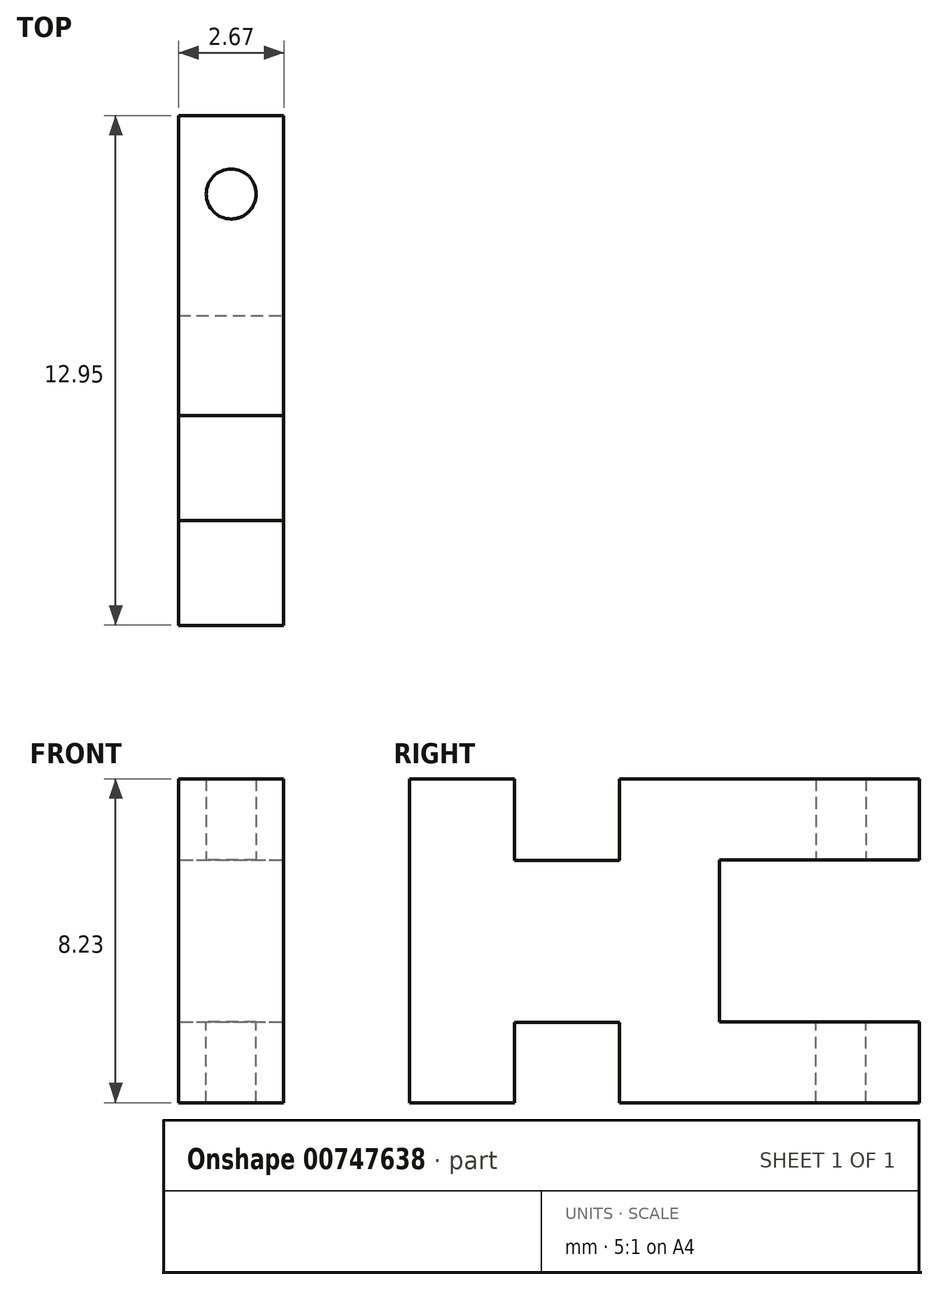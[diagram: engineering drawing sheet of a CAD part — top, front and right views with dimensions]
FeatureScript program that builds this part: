
annotation { "Feature Type Name" : "Feature", "Feature Type Description" : "" }
export const myFeature = defineFeature(function(context is Context, id is Id, definition is map)
    precondition{}
    {
        {
            var Q0;
            Q0=qCreatedBy(makeId("Right.planeOp"),FACE);
            var sketch = newSketch(context, id + "F0", { "sketchPlane" : qUnion([Q0])});
            skLineSegment(sketch, "E0.bottom", {"start": v(-1.33, 2.06) * mm, "end": v(1.33, 2.06) * mm});
            skLineSegment(sketch, "E0.top", {"start": v(-1.33, -2.06) * mm, "end": v(1.33, -2.06) * mm});
            skPoint(sketch, "E0.middle", {"position": v(0, 0) * mm});
            skLineSegment(sketch, "E1.bottom", {"start": v(-1.33, 4.13) * mm, "end": v(-4, 4.13) * mm});
            skLineSegment(sketch, "E1.top", {"start": v(-1.33, -4.1) * mm, "end": v(-4, -4.1) * mm});
            skLineSegment(sketch, "E1.left", {"start": v(-1.33, 4.13) * mm, "end": v(-1.33, 2.06) * mm});
            skLineSegment(sketch, "E1.right", {"start": v(-4, 4.13) * mm, "end": v(-4, -4.1) * mm});
            skPoint(sketch, "E2.firstSnap0", {"position": v(1.33, 0) * mm});
            skLineSegment(sketch, "E2.bottom", {"start": v(1.33, 4.13) * mm, "end": v(8.95, 4.13) * mm});
            skLineSegment(sketch, "E2.top", {"start": v(1.33, -4.1) * mm, "end": v(8.95, -4.1) * mm});
            skLineSegment(sketch, "E2.left", {"start": v(1.33, 4.13) * mm, "end": v(1.33, 2.06) * mm});
            skLineSegment(sketch, "E2.right", {"start": v(8.95, 4.13) * mm, "end": v(8.95, -4.1) * mm});
            skLineSegment(sketch, "E3.trimOffspring", {"start": v(-1.33, -2.06) * mm, "end": v(-1.33, -4.1) * mm});
            skLineSegment(sketch, "E4.trimOffspring", {"start": v(1.33, -2.06) * mm, "end": v(1.33, -4.1) * mm});
            skSolve(sketch);
        }
        {
            var Q0;
            {var subQ3=sQuery(id+"F0.wireOp",EDGE,"E2.bottom");Q0=makeQuery(id+"F0.imprint","IMPRINT",FACE,{"disambiguationData":[TD([[makeQuery(id+"F0.imprint","IMPRINT",EDGE,{"derivedFrom":subQ3}),-1.0]])]});}
            var Q1;
            {var subQ0=sQuery(id+"F0.wireOp",EDGE,"E0.bottom");Q1=makeQuery(id+"F0.imprint","IMPRINT",FACE,{"disambiguationData":[TD([[makeQuery(id+"F0.imprint","IMPRINT",EDGE,{"derivedFrom":subQ0}),-1.0]])]});}
            var Q2;
            {var subQ3=sQuery(id+"F0.wireOp",EDGE,"E1.bottom");Q2=makeQuery(id+"F0.imprint","IMPRINT",FACE,{"disambiguationData":[TD([[makeQuery(id+"F0.imprint","IMPRINT",EDGE,{"derivedFrom":subQ3}),1.0]])]});}
            extrude(context, id + "F1", {"entities" : qUnion([Q0, Q1, Q2]), "depth" : 2.67 * mm, "offsetDistance" : 25.4 * mm});
        }
        {
            var Q0;
            Q0=makeQuery(id+"F1.opExtrude","SWEPT_FACE",FACE,{"disambiguationData":[OSD([sQuery(id+"F0.wireOp",EDGE,"E2.right")])]});
            var sketch = newSketch(context, id + "F2", { "sketchPlane" : qUnion([Q0])});
            skLineSegment(sketch, "E5.bottom", {"start": v(0, 2.07) * mm, "end": v(-2.66, 2.07) * mm});
            skLineSegment(sketch, "E5.top", {"start": v(0, -2.05) * mm, "end": v(-2.66, -2.05) * mm});
            skLineSegment(sketch, "E5.left", {"start": v(0, 2.07) * mm, "end": v(0, -2.05) * mm});
            skLineSegment(sketch, "E5.right", {"start": v(-2.66, 2.07) * mm, "end": v(-2.66, -2.05) * mm});
            skSolve(sketch);
        }
        {
            var Q0;
            Q0=makeQuery(id+"F2.imprint","IMPRINT",FACE,{"disambiguationData":[TD([[makeQuery(id+"F2.imprint","IMPRINT",EDGE,{"derivedFrom":sQuery(id+"F2.wireOp",EDGE,"E5.bottom")}),1.0]])]});
            extrude(context, id + "F3", {"entities" : qUnion([Q0]), "operationType" : NewBodyOperationType.REMOVE, "oppositeDirection" : true, "depth" : 5.08 * mm, "offsetDistance" : 25.4 * mm});
        }
        {
            var Q0;
            Q0=makeQuery(id+"F3.boolean.opBoolean","COPY",FACE,{"derivedFrom":makeQuery(id+"F3.opExtrude","SWEPT_FACE",FACE,{"disambiguationData":[OSD([sQuery(id+"F2.wireOp",EDGE,"E5.top")])]})});
            var sketch = newSketch(context, id + "F4", { "sketchPlane" : qUnion([Q0])});
            skPoint(sketch, "E6.endSnap0", {"position": v(0, 6.41) * mm});
            skCircle(sketch, "E7", {"center": v(1.33, 6.96) * mm, "radius": 0.64 * mm});
            skSolve(sketch);
        }
        {
            var Q0;
            Q0=makeQuery(id+"F4.imprint","IMPRINT",FACE,{"disambiguationData":[TD([[makeQuery(id+"F4.imprint","IMPRINT",EDGE,{"derivedFrom":sQuery(id+"F4.wireOp",EDGE,"E7")}),1.0]])]});
            extrude(context, id + "F5", {"entities" : qUnion([Q0]), "operationType" : NewBodyOperationType.REMOVE, "depth" : 25.4 * mm, "offsetDistance" : 25.4 * mm});
        }
        {
            var Q0;
            Q0=makeQuery(id+"F3.boolean.opBoolean","COPY",FACE,{"derivedFrom":makeQuery(id+"F3.opExtrude","SWEPT_FACE",FACE,{"disambiguationData":[OSD([sQuery(id+"F2.wireOp",EDGE,"E5.top")])]})});
            var sketch = newSketch(context, id + "F6", { "sketchPlane" : qUnion([Q0])});
            skCircle(sketch, "E8", {"center": v(1.33, 6.96) * mm, "radius": 0.64 * mm});
            skSolve(sketch);
        }
        {
            var Q0;
            Q0=makeQuery(id+"F6.imprint","IMPRINT",FACE,{"disambiguationData":[TD([[makeQuery(id+"F6.imprint","IMPRINT",EDGE,{"derivedFrom":sQuery(id+"F6.wireOp",EDGE,"E8")}),1.0]])]});
            extrude(context, id + "F7", {"entities" : qUnion([Q0]), "operationType" : NewBodyOperationType.REMOVE, "oppositeDirection" : true, "depth" : 25.4 * mm, "offsetDistance" : 25.4 * mm});
        }
    });
